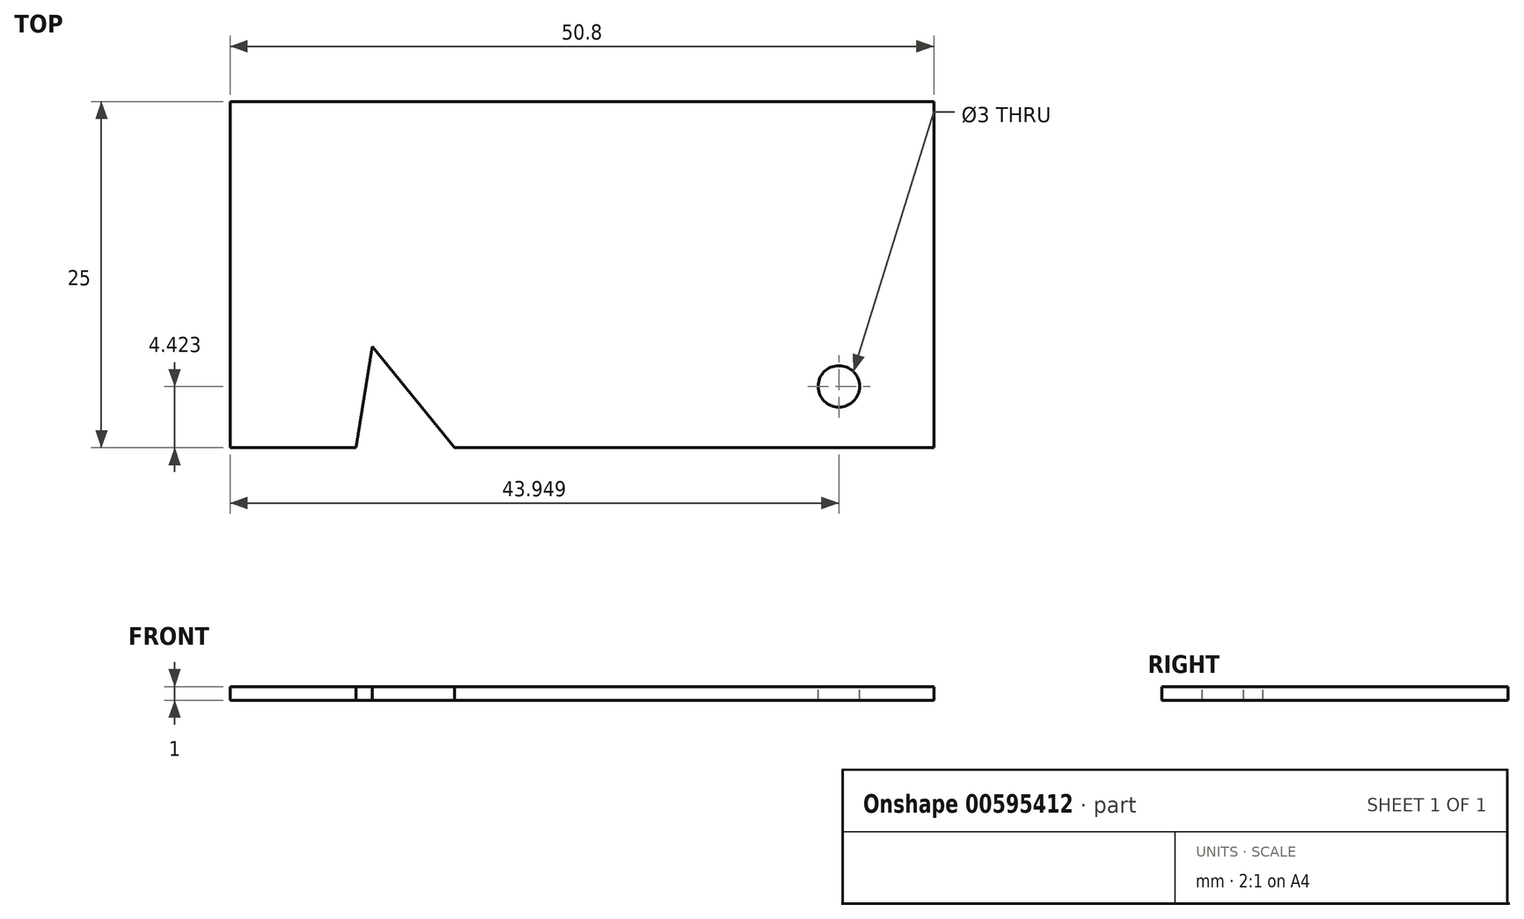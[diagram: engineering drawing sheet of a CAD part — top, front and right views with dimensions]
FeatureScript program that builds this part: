
annotation { "Feature Type Name" : "Feature", "Feature Type Description" : "" }
export const myFeature = defineFeature(function(context is Context, id is Id, definition is map)
    precondition{}
    {
        {
            var Q0;
            Q0=qCreatedBy(makeId("Top.planeOp"),FACE);
            var sketch = newSketch(context, id + "F0", { "sketchPlane" : qUnion([Q0])});
            skLineSegment(sketch, "E0.bottom", {"start": v(-25.4, 12.5) * mm, "end": v(25.4, 12.5) * mm});
            skLineSegment(sketch, "E0.top", {"start": v(-25.4, -12.5) * mm, "end": v(25.4, -12.5) * mm});
            skLineSegment(sketch, "E0.left", {"start": v(-25.4, 12.5) * mm, "end": v(-25.4, -12.5) * mm});
            skLineSegment(sketch, "E0.right", {"start": v(25.4, 12.5) * mm, "end": v(25.4, -12.5) * mm});
            skPoint(sketch, "E0.middle", {"position": v(0, 0) * mm});
            skSolve(sketch);
        }
        {
            var Q0;
            Q0 = qSketchRegion(id + "F0", true);
            extrude(context, id + "F1", {"entities" : qUnion([Q0]), "depth" : 1 * mm, "offsetDistance" : 25 * mm});
        }
        {
            var Q0;
            Q0=makeQuery(id+"F1.opExtrude","CAP_FACE",FACE,{"disambiguationData":[OSD([sQuery(id+"F0.wireOp",EDGE,"E0.bottom"),sQuery(id+"F0.wireOp",EDGE,"E0.top"),sQuery(id+"F0.wireOp",EDGE,"E0.left"),sQuery(id+"F0.wireOp",EDGE,"E0.right")])],"isStart":false});
            var sketch = newSketch(context, id + "F2", { "sketchPlane" : qUnion([Q0])});
            skCircle(sketch, "E1", {"center": v(18.55, -8.08) * mm, "radius": 1.5 * mm});
            skSolve(sketch);
        }
        {
            var Q0;
            Q0 = qSketchRegion(id + "F2", true);
            extrude(context, id + "F3", {"entities" : qUnion([Q0]), "operationType" : NewBodyOperationType.REMOVE, "oppositeDirection" : true, "depth" : 25 * mm, "offsetDistance" : 25 * mm});
        }
        {
            var Q0;
            Q0=makeQuery(id+"F1.opExtrude","CAP_FACE",FACE,{"disambiguationData":[OSD([sQuery(id+"F0.wireOp",EDGE,"E0.bottom"),sQuery(id+"F0.wireOp",EDGE,"E0.top"),sQuery(id+"F0.wireOp",EDGE,"E0.left"),sQuery(id+"F0.wireOp",EDGE,"E0.right")])],"isStart":false});
            var sketch = newSketch(context, id + "F4", { "sketchPlane" : qUnion([Q0])});
            skLineSegment(sketch, "E2", {"start": v(-16.32, -12.5) * mm, "end": v(-15.13, -5.2) * mm});
            skLineSegment(sketch, "E3", {"start": v(-15.13, -5.2) * mm, "end": v(-9.2, -12.5) * mm});
            skLineSegment(sketch, "E4", {"start": v(-9.2, -12.5) * mm, "end": v(-6.96, -5.2) * mm});
            skLineSegment(sketch, "E5", {"start": v(-6.96, -5.2) * mm, "end": v(-1.03, -12.5) * mm});
            skLineSegment(sketch, "E6", {"start": v(0, -12.5) * mm, "end": v(1.38, -5.2) * mm});
            skLineSegment(sketch, "E7", {"start": v(1.38, -5.2) * mm, "end": v(7.31, -12.5) * mm});
            skLineSegment(sketch, "E8", {"start": v(-16.32, -12.5) * mm, "end": v(-12.45, -21.5) * mm});
            skLineSegment(sketch, "E9", {"start": v(-12.45, -21.5) * mm, "end": v(-9.2, -13.53) * mm});
            skLineSegment(sketch, "E10", {"start": v(-9.2, -12.5) * mm, "end": v(0, -20.38) * mm});
            skLineSegment(sketch, "E11", {"start": v(0, -20.38) * mm, "end": v(0, -12.5) * mm});
            skLineSegment(sketch, "E12", {"start": v(0, -13.46) * mm, "end": v(8.25, -20.38) * mm});
            skLineSegment(sketch, "E13", {"start": v(8.25, -20.38) * mm, "end": v(8.25, -13.6) * mm});
            skLineSegment(sketch, "E14", {"start": v(8.25, -13.6) * mm, "end": v(7.31, -12.5) * mm});
            skSolve(sketch);
        }
        {
            var Q0;
            {var subQ0=sQuery(id+"F4.wireOp",EDGE,"E2");Q0=makeQuery(id+"F4.imprint","IMPRINT",FACE,{"disambiguationData":[TD([[makeQuery(id+"F4.imprint","IMPRINT",EDGE,{"derivedFrom":subQ0}),-1.0]])]});}
            extrude(context, id + "F5", {"entities" : qUnion([Q0]), "operationType" : NewBodyOperationType.REMOVE, "oppositeDirection" : true, "depth" : 25 * mm, "offsetDistance" : 25 * mm});
        }
    });
